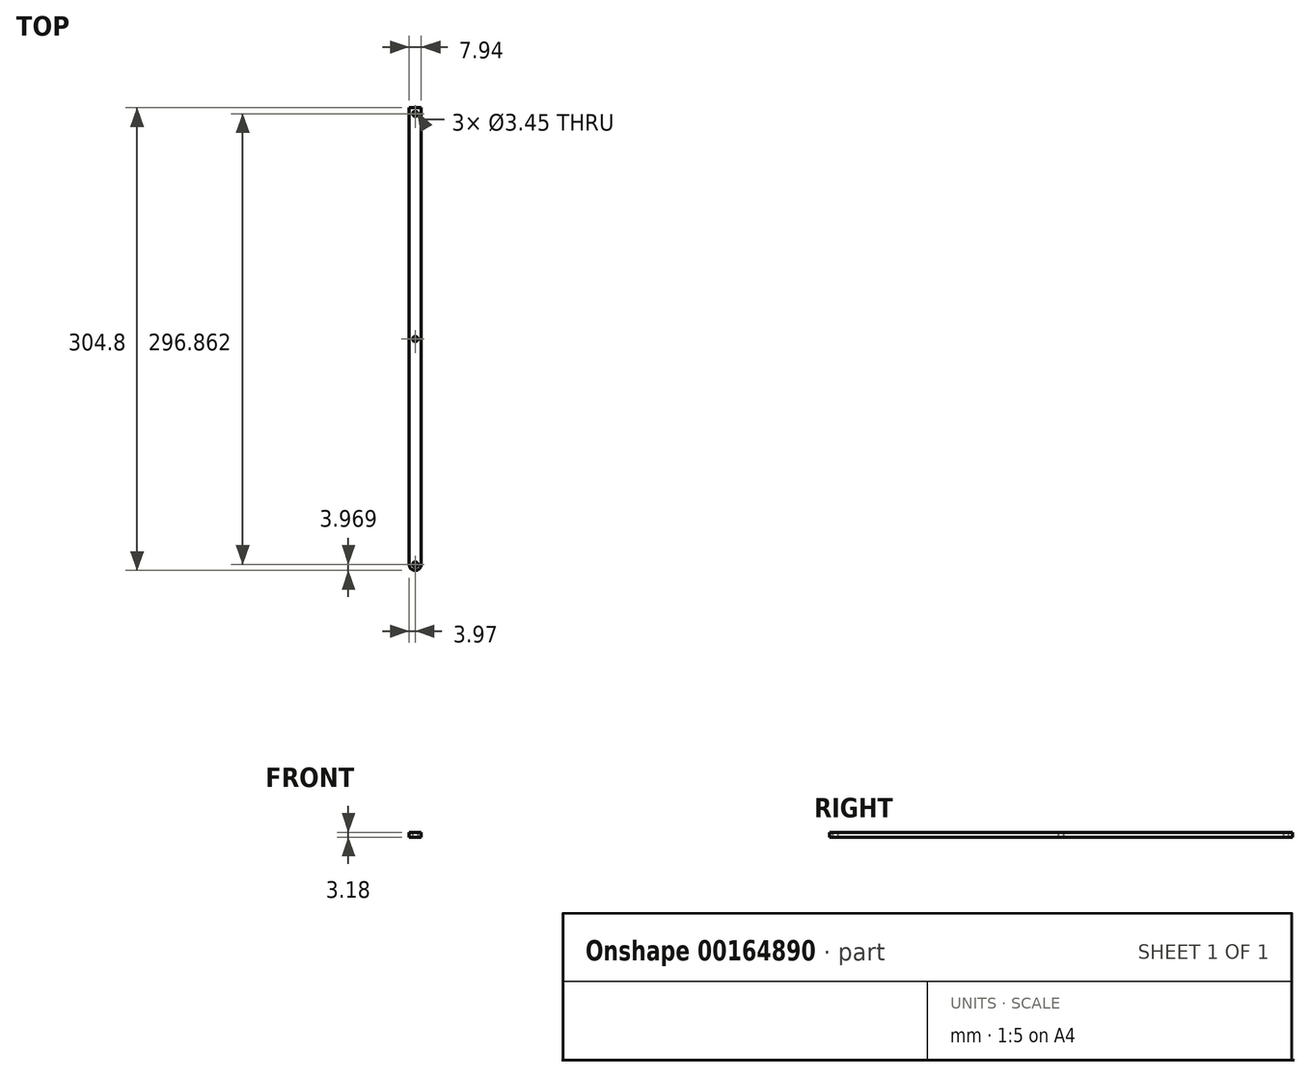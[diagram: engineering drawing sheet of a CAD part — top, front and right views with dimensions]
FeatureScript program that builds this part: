
annotation { "Feature Type Name" : "Feature", "Feature Type Description" : "" }
export const myFeature = defineFeature(function(context is Context, id is Id, definition is map)
    precondition{}
    {
        {
            var Q0;
            Q0=qCreatedBy(makeId("Top.planeOp"),FACE);
            var sketch = newSketch(context, id + "F0", { "sketchPlane" : qUnion([Q0])});
            skLineSegment(sketch, "E0.bottom", {"start": v(3.97, -152.4) * mm, "end": v(-3.97, -152.4) * mm});
            skLineSegment(sketch, "E0.top", {"start": v(3.97, 152.4) * mm, "end": v(-3.97, 152.4) * mm});
            skLineSegment(sketch, "E0.left", {"start": v(3.97, -152.4) * mm, "end": v(3.97, 152.4) * mm});
            skLineSegment(sketch, "E0.right", {"start": v(-3.97, -152.4) * mm, "end": v(-3.97, 152.4) * mm});
            skPoint(sketch, "E0.middle", {"position": v(0, 0) * mm});
            skCircle(sketch, "E1", {"center": v(0, 0) * mm, "radius": 1.73 * mm});
            skSolve(sketch);
        }
        {
            var Q0;
            Q0 = qSketchRegion(id + "F0", true);
            extrude(context, id + "F1", {"entities" : qUnion([Q0]), "depth" : 3.17 * mm});
        }
        {
            var Q0;
            Q0=makeQuery(id+"F1.opExtrude","CAP_FACE",FACE,{"disambiguationData":[OSD([sQuery(id+"F0.wireOp",EDGE,"E0.bottom"),sQuery(id+"F0.wireOp",EDGE,"E0.top"),sQuery(id+"F0.wireOp",EDGE,"E0.left"),sQuery(id+"F0.wireOp",EDGE,"E0.right"),sQuery(id+"F0.wireOp",EDGE,"E1")])],"isStart":false});
            var sketch = newSketch(context, id + "F2", { "sketchPlane" : qUnion([Q0])});
            skLineSegment(sketch, "E2.bottom", {"start": v(0, 152.4) * mm, "end": v(3.97, 152.4) * mm, "construction": true});
            skLineSegment(sketch, "E2.top", {"start": v(0, 148.43) * mm, "end": v(3.97, 148.43) * mm, "construction": true});
            skLineSegment(sketch, "E2.left", {"start": v(0, 152.4) * mm, "end": v(0, 148.43) * mm, "construction": true});
            skLineSegment(sketch, "E2.right", {"start": v(3.97, 152.4) * mm, "end": v(3.97, 148.43) * mm, "construction": true});
            skLineSegment(sketch, "E3.bottom", {"start": v(0, -152.4) * mm, "end": v(3.97, -152.4) * mm, "construction": true});
            skLineSegment(sketch, "E3.top", {"start": v(0, -148.43) * mm, "end": v(3.97, -148.43) * mm, "construction": true});
            skLineSegment(sketch, "E3.left", {"start": v(0, -152.4) * mm, "end": v(0, -148.43) * mm, "construction": true});
            skLineSegment(sketch, "E3.right", {"start": v(3.97, -152.4) * mm, "end": v(3.97, -148.43) * mm, "construction": true});
            skCircle(sketch, "E4", {"center": v(0, 148.43) * mm, "radius": 1.73 * mm});
            skCircle(sketch, "E5", {"center": v(0, -148.43) * mm, "radius": 1.73 * mm});
            skSolve(sketch);
        }
        {
            var Q0;
            Q0 = qSketchRegion(id + "F2", true);
            var Q1;
            Q1=makeQuery(id+"F1.opExtrude","CAP_FACE",FACE,{"disambiguationData":[OSD([sQuery(id+"F0.wireOp",EDGE,"E0.bottom"),sQuery(id+"F0.wireOp",EDGE,"E0.top"),sQuery(id+"F0.wireOp",EDGE,"E0.left"),sQuery(id+"F0.wireOp",EDGE,"E0.right"),sQuery(id+"F0.wireOp",EDGE,"E1")])],"isStart":true});
            extrude(context, id + "F3", {"entities" : qUnion([Q0]), "operationType" : NewBodyOperationType.REMOVE, "endBound" : BoundingType.UP_TO_SURFACE, "oppositeDirection" : true, "endBoundEntityFace" : qUnion([Q1]), "depth" : 25.4 * mm});
        }
        {
            var Q0;
            Q0=makeQuery(id+"F1.opExtrude","SWEPT_EDGE",EDGE,{"disambiguationData":[OSD([sQuery(id+"F0.wireOp",EDGE,"E0.bottom"),sQuery(id+"F0.wireOp",EDGE,"E0.right")])]});
            var Q1;
            Q1=makeQuery(id+"F1.opExtrude","SWEPT_EDGE",EDGE,{"disambiguationData":[OSD([sQuery(id+"F0.wireOp",EDGE,"E0.bottom"),sQuery(id+"F0.wireOp",EDGE,"E0.left")])]});
            fillet(context, id + "F4", {"entities" : qUnion([Q0, Q1]), "radius" : 3.97 * mm, "tangentPropagation" : true, "allowEdgeOverflow" : false});
        }
    });
